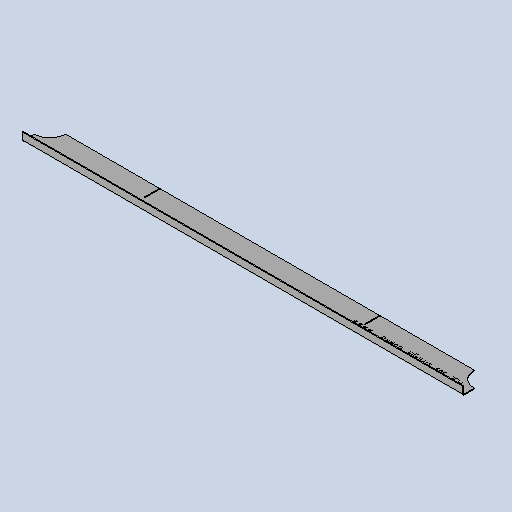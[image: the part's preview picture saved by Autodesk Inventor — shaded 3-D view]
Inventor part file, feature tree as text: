
AUTODESK INVENTOR PART (.ipt)
format: ipt  version: 2025 (Build 290162010, 162A)  size: 303,104 bytes
history: native  units: mm
features: other x5, sheet_metal_op x4, sketch x4, extrude x1
ambient origin geometry x8: Origin, YZ Plane, XZ Plane, XY Plane, X Axis, Y Axis, Z Axis, Center Point
bodies: Solid1 (feature_tree)
feature tree (14):
  sheet_metal_op  "Face1"
  sheet_metal_op  "Flange1"
  extrude  "Extrusion1"  Depth=62.0mm
  other  "Mark2"
  other  "A-Side Definition"
  sketch  "Sketch1"  dims[d0=980.0mm d1=62.0mm]
  other  "Plate1"
  sketch  "Sketch2"  dims[d2=2.0mm]
  other  "Plate2"
  sheet_metal_op  "Bend1"
  sheet_metal_op  "Corner1"
  sketch  "Sketch5"  dims[d3=2.0mm]
  sketch  "Sketch9"  dims[d4=1.0mm d5=4.0mm d6=2.75mm d7=20.0mm d8=90.0deg d9=2.75mm d10=8.0mm d11=2.0mm d12=2.75mm d15=0.0mm d16=0.0mm d40=200.0mm d41=12.0mm d45=70.0mm d48=2.1mm d49=490.0mm d51=29.0mm d52=33.0mm]
  other  "Definition1"
